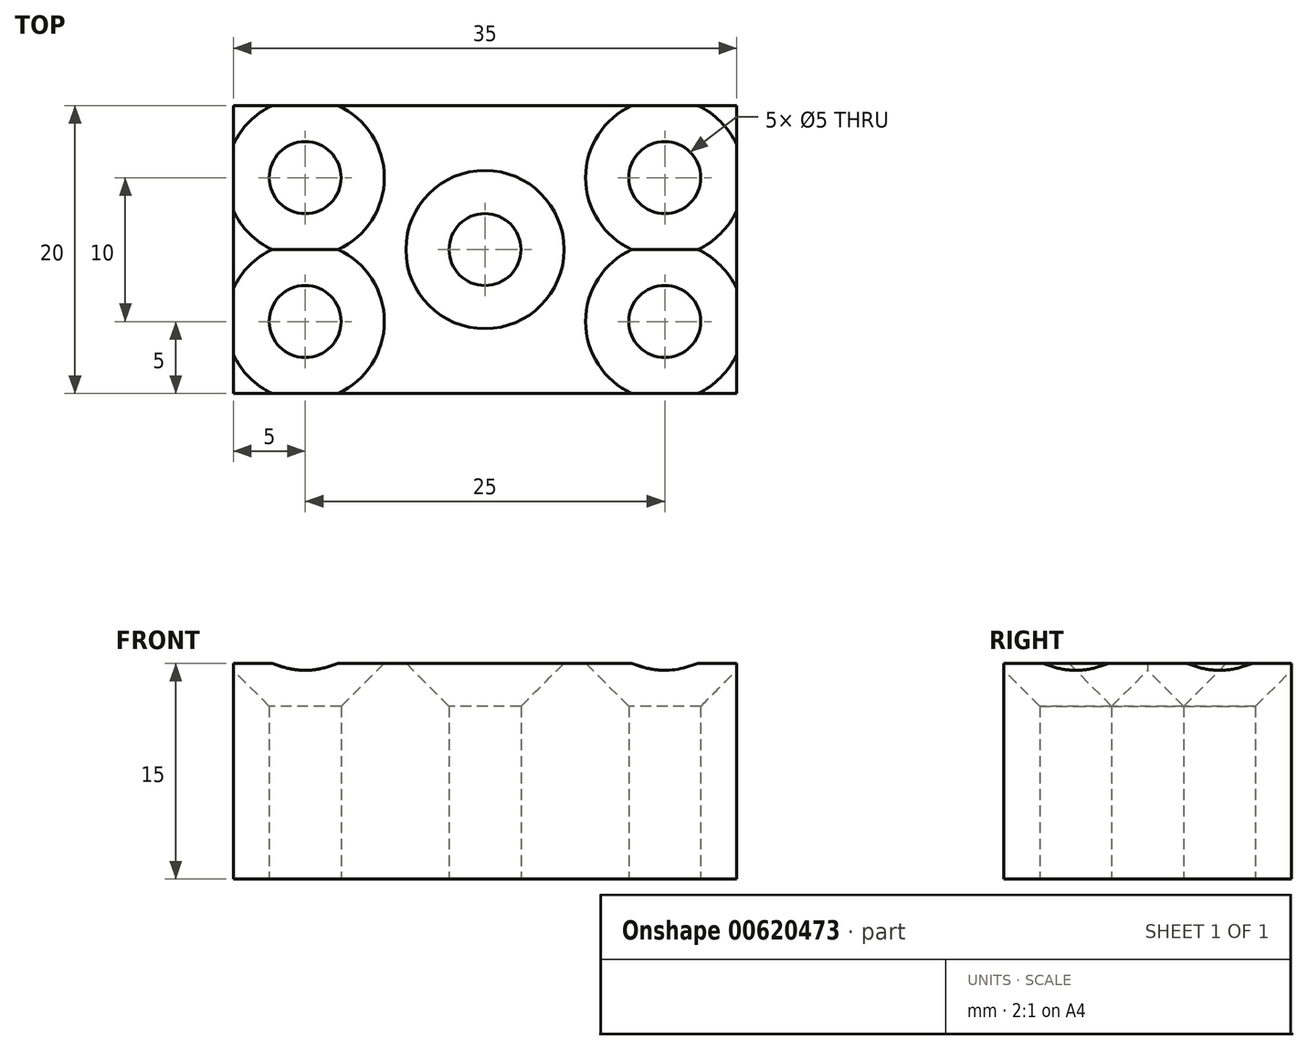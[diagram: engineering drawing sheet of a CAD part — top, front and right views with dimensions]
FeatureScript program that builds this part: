
annotation { "Feature Type Name" : "Feature", "Feature Type Description" : "" }
export const myFeature = defineFeature(function(context is Context, id is Id, definition is map)
    precondition{}
    {
        {
            var Q0;
            Q0=qCreatedBy(makeId("Top.planeOp"),FACE);
            var sketch = newSketch(context, id + "F0", { "sketchPlane" : qUnion([Q0])});
            skCircle(sketch, "E0", {"center": v(0, 0) * mm, "radius": 2.5 * mm});
            skLineSegment(sketch, "E1.bottom", {"start": v(-17.5, 10) * mm, "end": v(17.5, 10) * mm});
            skLineSegment(sketch, "E1.top", {"start": v(-17.5, -10) * mm, "end": v(17.5, -10) * mm});
            skLineSegment(sketch, "E1.left", {"start": v(-17.5, 10) * mm, "end": v(-17.5, -10) * mm});
            skLineSegment(sketch, "E1.right", {"start": v(17.5, 10) * mm, "end": v(17.5, -10) * mm});
            skLineSegment(sketch, "E2", {"start": v(-7.5, 10) * mm, "end": v(-7.5, -10) * mm, "construction": true});
            skLineSegment(sketch, "E3", {"start": v(-17.5, 5) * mm, "end": v(-7.5, 5) * mm, "construction": true});
            skLineSegment(sketch, "E4", {"start": v(-17.5, 10) * mm, "end": v(-7.5, 10) * mm});
            skLineSegment(sketch, "E5", {"start": v(-17.5, 10) * mm, "end": v(-17.5, 5) * mm});
            skLineSegment(sketch, "E6", {"start": v(-17.5, 5) * mm, "end": v(-7.5, 5) * mm});
            skCircle(sketch, "E7", {"center": v(-12.5, 5) * mm, "radius": 2.5 * mm});
            skCircle(sketch, "E8.MirrorC", {"center": v(-12.5, -5) * mm, "radius": 2.5 * mm});
            skCircle(sketch, "E9.MirrorC", {"center": v(12.5, 5) * mm, "radius": 2.5 * mm});
            skCircle(sketch, "E10.MirrorC", {"center": v(12.5, -5) * mm, "radius": 2.5 * mm});
            skSolve(sketch);
        }
        {
            var Q0;
            Q0 = qSketchRegion(id + "F0", true);
            extrude(context, id + "F1", {"entities" : qUnion([Q0]), "depth" : 15 * mm, "offsetDistance" : 25 * mm});
        }
        {
            var Q0;
            Q0=makeQuery(id+"F1.opExtrude","CAP_EDGE",EDGE,{"disambiguationData":[OSD([sQuery(id+"F0.wireOp",EDGE,"E7")])],"isStart":false});
            var Q1;
            Q1=makeQuery(id+"F1.opExtrude","CAP_EDGE",EDGE,{"disambiguationData":[OSD([sQuery(id+"F0.wireOp",EDGE,"E0")])],"isStart":false});
            var Q2;
            Q2=makeQuery(id+"F1.opExtrude","CAP_EDGE",EDGE,{"disambiguationData":[OSD([sQuery(id+"F0.wireOp",EDGE,"E8.MirrorC")])],"isStart":false});
            var Q3;
            Q3=makeQuery(id+"F1.opExtrude","CAP_EDGE",EDGE,{"disambiguationData":[OSD([sQuery(id+"F0.wireOp",EDGE,"E9.MirrorC")])],"isStart":false});
            var Q4;
            Q4=makeQuery(id+"F1.opExtrude","CAP_EDGE",EDGE,{"disambiguationData":[OSD([sQuery(id+"F0.wireOp",EDGE,"E10.MirrorC")])],"isStart":false});
            chamfer(context, id + "F2", {"entities" : qUnion([Q0, Q1, Q2, Q3, Q4]), "width" : 3 * mm, "tangentPropagation" : true});
        }
    });
